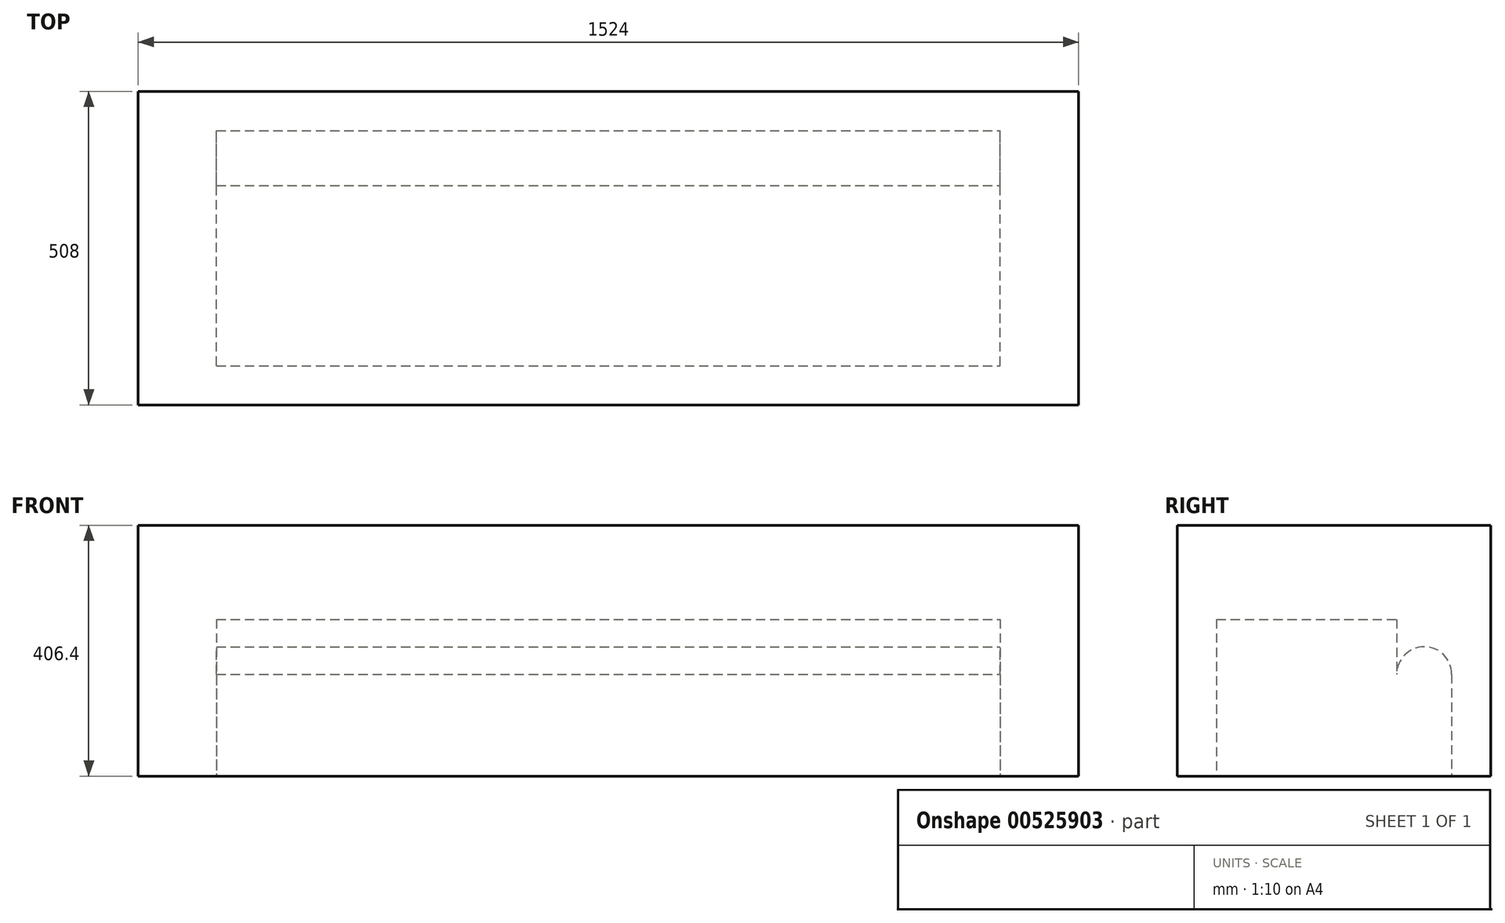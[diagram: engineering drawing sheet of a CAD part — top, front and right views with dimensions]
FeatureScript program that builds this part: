
annotation { "Feature Type Name" : "Feature", "Feature Type Description" : "" }
export const myFeature = defineFeature(function(context is Context, id is Id, definition is map)
    precondition{}
    {
        {
            var Q0;
            Q0=qCreatedBy(makeId("Top.planeOp"),FACE);
            var sketch = newSketch(context, id + "F0", { "sketchPlane" : qUnion([Q0])});
            skLineSegment(sketch, "E0.bottom", {"start": v(762, 254) * mm, "end": v(-762, 254) * mm});
            skLineSegment(sketch, "E0.top", {"start": v(762, -254) * mm, "end": v(-762, -254) * mm});
            skLineSegment(sketch, "E0.left", {"start": v(762, 254) * mm, "end": v(762, -254) * mm});
            skLineSegment(sketch, "E0.right", {"start": v(-762, 254) * mm, "end": v(-762, -254) * mm});
            skPoint(sketch, "E0.middle", {"position": v(0, 0) * mm});
            skSolve(sketch);
        }
        {
            var Q0;
            Q0 = qSketchRegion(id + "F0", true);
            extrude(context, id + "F1", {"entities" : qUnion([Q0]), "depth" : 381 * mm, "offsetDistance" : 25.4 * mm});
        }
        {
            var Q0;
            Q0=makeQuery(id+"F1.opExtrude","CAP_FACE",FACE,{"disambiguationData":[OSD([sQuery(id+"F0.wireOp",EDGE,"E0.bottom"),sQuery(id+"F0.wireOp",EDGE,"E0.top"),sQuery(id+"F0.wireOp",EDGE,"E0.left"),sQuery(id+"F0.wireOp",EDGE,"E0.right")])],"isStart":true});
            var sketch = newSketch(context, id + "F2", { "sketchPlane" : qUnion([Q0])});
            skLineSegment(sketch, "E1.bottom", {"start": v(-635, 190.5) * mm, "end": v(635, 190.5) * mm});
            skLineSegment(sketch, "E1.top", {"start": v(-635, -190.5) * mm, "end": v(635, -190.5) * mm});
            skLineSegment(sketch, "E1.left", {"start": v(-635, 190.5) * mm, "end": v(-635, -190.5) * mm});
            skLineSegment(sketch, "E1.right", {"start": v(635, 190.5) * mm, "end": v(635, -190.5) * mm});
            skPoint(sketch, "E1.middle", {"position": v(0, 0) * mm});
            skLineSegment(sketch, "E2", {"start": v(0, -190.5) * mm, "end": v(0, -254) * mm, "construction": true});
            skLineSegment(sketch, "E3", {"start": v(635, 0) * mm, "end": v(762, 0) * mm, "construction": true});
            skSolve(sketch);
        }
        {
            var Q0;
            Q0 = qSketchRegion(id + "F2", true);
            extrude(context, id + "F3", {"entities" : qUnion([Q0]), "operationType" : NewBodyOperationType.REMOVE, "oppositeDirection" : true, "depth" : 254 * mm, "offsetDistance" : 25.4 * mm});
        }
        {
            var Q0;
            Q0=makeQuery(id+"F3.boolean.opBoolean","COPY",FACE,{"derivedFrom":makeQuery(id+"F3.opExtrude","SWEPT_FACE",FACE,{"disambiguationData":[OSD([sQuery(id+"F2.wireOp",EDGE,"E1.right")])]})});
            var sketch = newSketch(context, id + "F4", { "sketchPlane" : qUnion([Q0])});
            skLineSegment(sketch, "E4.bottom", {"start": v(-190.5, 254) * mm, "end": v(-101.6, 254) * mm});
            skLineSegment(sketch, "E4.left", {"start": v(-190.5, 254) * mm, "end": v(-190.5, 165.1) * mm});
            skLineSegment(sketch, "E4.right", {"start": v(-101.6, 254) * mm, "end": v(-101.6, 165.1) * mm});
            skArc(sketch, "E5", {"start": v(-101.6, 165.1) * mm, "mid": v(-146.05, 209.55) * mm, "end": v(-190.5, 165.1) * mm});
            skSolve(sketch);
        }
        {
            var Q0;
            Q0=makeQuery(id+"F4.imprint","IMPRINT",FACE,{"disambiguationData":[TD([[makeQuery(id+"F4.imprint","IMPRINT",EDGE,{"derivedFrom":sQuery(id+"F4.wireOp",EDGE,"E4.bottom")}),1.0]])]});
            extrude(context, id + "F5", {"entities" : qUnion([Q0]), "operationType" : NewBodyOperationType.ADD, "endBound" : BoundingType.UP_TO_NEXT, "depth" : 25.4 * mm, "offsetDistance" : 25.4 * mm});
        }
        {
            var Q0;
            Q0=makeQuery(id+"F1.opExtrude","CAP_FACE",FACE,{"disambiguationData":[OSD([sQuery(id+"F0.wireOp",EDGE,"E0.bottom"),sQuery(id+"F0.wireOp",EDGE,"E0.top"),sQuery(id+"F0.wireOp",EDGE,"E0.left"),sQuery(id+"F0.wireOp",EDGE,"E0.right")])],"isStart":false});
            var sketch = newSketch(context, id + "F6", { "sketchPlane" : qUnion([Q0])});
            skSolve(sketch);
        }
        {
            var Q0;
            Q0=makeQuery(id+"F6.imprint","IMPRINT",FACE,{"disambiguationData":[TD([[makeQuery(id+"F6.imprint","IMPRINT",EDGE,{"derivedFrom":makeQuery(id+"F1.opExtrude","CAP_EDGE",EDGE,{"disambiguationData":[OSD([sQuery(id+"F0.wireOp",EDGE,"E0.bottom")])],"isStart":false})}),1.0]])]});
            extrude(context, id + "F7", {"entities" : qUnion([Q0]), "operationType" : NewBodyOperationType.ADD, "depth" : 25.4 * mm, "offsetDistance" : 25.4 * mm});
        }
    });
